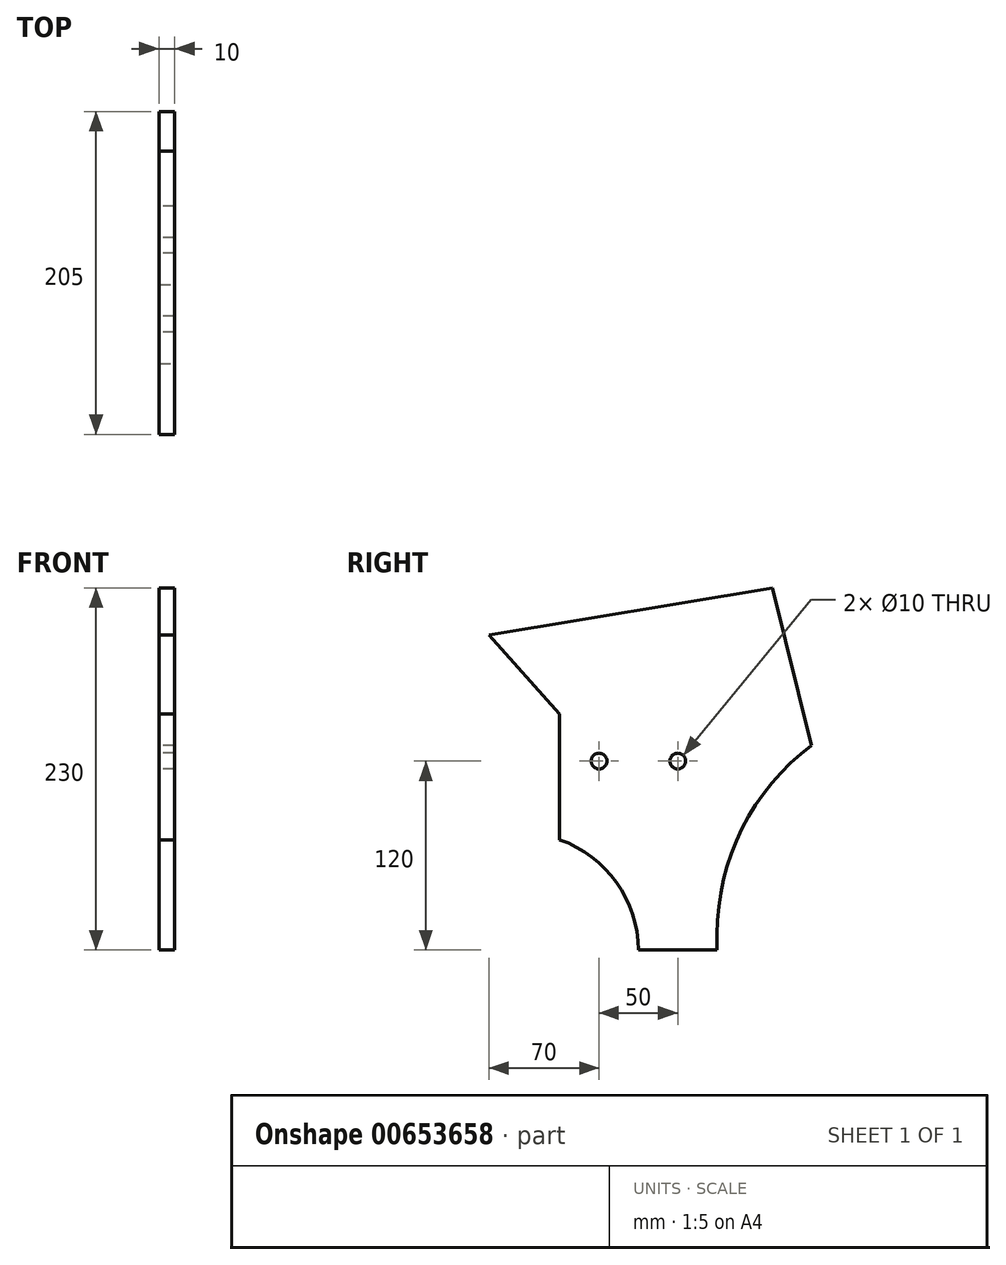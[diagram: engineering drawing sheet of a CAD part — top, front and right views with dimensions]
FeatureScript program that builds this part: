
annotation { "Feature Type Name" : "Feature", "Feature Type Description" : "" }
export const myFeature = defineFeature(function(context is Context, id is Id, definition is map)
    precondition{}
    {
        {
            var Q0;
            Q0=qCreatedBy(makeId("Right.planeOp"),FACE);
            var sketch = newSketch(context, id + "F0", { "sketchPlane" : qUnion([Q0])});
            skLineSegment(sketch, "E0.bottom", {"start": v(0, 0) * mm, "end": v(100, 0) * mm});
            skLineSegment(sketch, "E0.top", {"start": v(0, 200) * mm, "end": v(100, 200) * mm});
            skLineSegment(sketch, "E0.left", {"start": v(0, 0) * mm, "end": v(0, 200) * mm});
            skLineSegment(sketch, "E0.right", {"start": v(100, 0) * mm, "end": v(100, 200) * mm});
            skLineSegment(sketch, "E1", {"start": v(0, 150) * mm, "end": v(-45, 200) * mm});
            skLineSegment(sketch, "E2", {"start": v(-45, 200) * mm, "end": v(135, 230) * mm});
            skLineSegment(sketch, "E3", {"start": v(135, 230) * mm, "end": v(160, 130) * mm});
            skLineSegment(sketch, "E4", {"start": v(160, 130) * mm, "end": v(100, 100) * mm});
            skSolve(sketch);
        }
        {
            var Q0;
            Q0 = qSketchRegion(id + "F0", true);
            extrude(context, id + "F1", {"entities" : qUnion([Q0]), "depth" : 10 * mm, "offsetDistance" : 25 * mm});
        }
        {
            var Q0;
            Q0=makeQuery(id+"F1.opExtrude","CAP_FACE",FACE,{"disambiguationData":[OSD([sQuery(id+"F0.wireOp",EDGE,"E0.bottom"),sQuery(id+"F0.wireOp",EDGE,"E0.top"),sQuery(id+"F0.wireOp",EDGE,"E0.left"),sQuery(id+"F0.wireOp",EDGE,"E0.right")])],"isStart":false});
            var sketch = newSketch(context, id + "F2", { "sketchPlane" : qUnion([Q0])});
            skPoint(sketch, "E5", {"position": v(25, 120) * mm});
            skPoint(sketch, "E6", {"position": v(75, 120) * mm});
            skSolve(sketch);
        }
        {
            var Q0;
            Q0=sQuery(id+"F2.wireOp",VERTEX,"E5");
            var Q1;
            Q1=sQuery(id+"F2.wireOp",VERTEX,"E6");
            var Q2;
            Q2=makeQuery(id+"F1.opExtrude","SWEPT_BODY",BODY,{"disambiguationData":[OSD([sQuery(id+"F0.wireOp",EDGE,"E0.bottom"),sQuery(id+"F0.wireOp",EDGE,"E0.top"),sQuery(id+"F0.wireOp",EDGE,"E0.left"),sQuery(id+"F0.wireOp",EDGE,"E0.right")])]});
            hole(context, id + "F3", {"style" : HoleStyle.SIMPLE, "endStyle" : HoleEndStyle.BLIND, "holeDiameter" : 10 * mm, "majorDiameter" : 5 * mm, "holeDepth" : 100 * mm, "isTappedThrough" : true, "tappedDepth" : 12 * mm, "tapClearance" : 3, "locations" : qUnion([Q0, Q1]), "scope" : qUnion([Q2])});
        }
        {
            var Q0;
            Q0=makeQuery(id+"F1.opExtrude","CAP_FACE",FACE,{"disambiguationData":[OSD([sQuery(id+"F0.wireOp",EDGE,"E0.bottom"),sQuery(id+"F0.wireOp",EDGE,"E0.top"),sQuery(id+"F0.wireOp",EDGE,"E0.left"),sQuery(id+"F0.wireOp",EDGE,"E0.right")])],"isStart":false});
            var sketch = newSketch(context, id + "F4", { "sketchPlane" : qUnion([Q0])});
            skArc(sketch, "E7", {"start": v(50, 0) * mm, "mid": v(36.03, 42.88) * mm, "end": v(0, 70) * mm});
            skSolve(sketch);
        }
        {
            var Q0;
            {var subQ0=sQuery(id+"F4.wireOp",EDGE,"E7");Q0=makeQuery(id+"F4.imprint","IMPRINT",FACE,{"disambiguationData":[TD([[makeQuery(id+"F4.imprint","IMPRINT",EDGE,{"derivedFrom":subQ0}),1.0]])]});}
            extrude(context, id + "F5", {"entities" : qUnion([Q0]), "operationType" : NewBodyOperationType.REMOVE, "oppositeDirection" : true, "depth" : 25 * mm, "offsetDistance" : 25 * mm});
        }
        {
            var Q0;
            Q0=makeQuery(id+"F1.opExtrude","SWEPT_EDGE",EDGE,{"disambiguationData":[OSD([sQuery(id+"F0.wireOp",EDGE,"E0.right"),sQuery(id+"F0.wireOp",EDGE,"E4")])]});
            fillet(context, id + "F6", {"entities" : qUnion([Q0]), "radius" : 150 * mm, "tangentPropagation" : true, "allowEdgeOverflow" : false});
        }
    });
